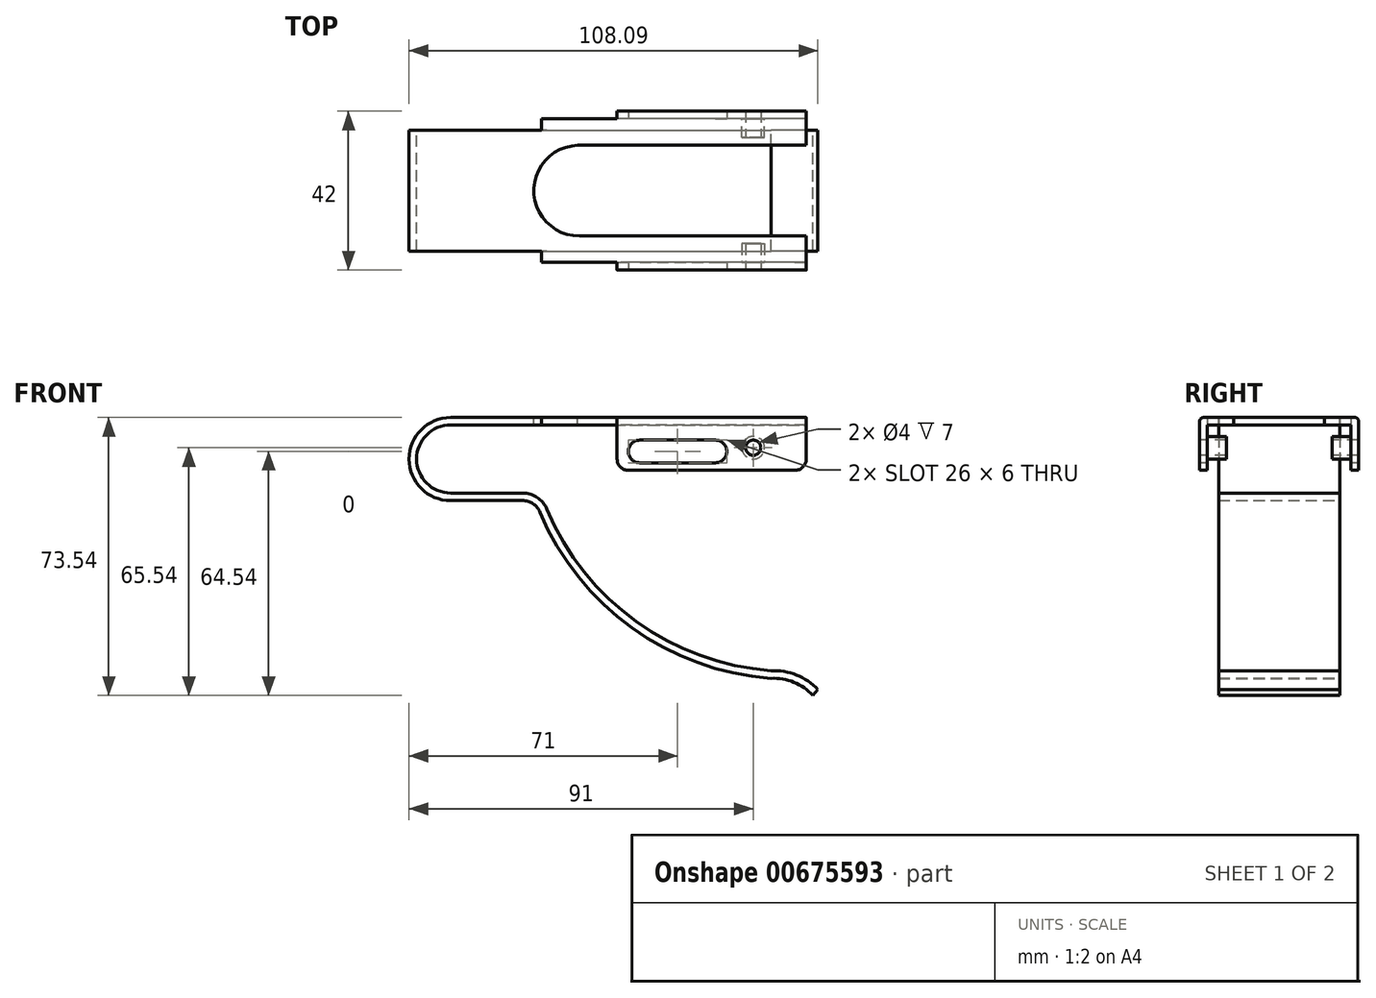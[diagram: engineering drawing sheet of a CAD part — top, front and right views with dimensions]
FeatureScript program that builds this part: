
annotation { "Feature Type Name" : "Feature", "Feature Type Description" : "" }
export const myFeature = defineFeature(function(context is Context, id is Id, definition is map)
    precondition{}
    {
        {
            var Q0;
            Q0=qCreatedBy(makeId("Front.planeOp"),FACE);
            var sketch = newSketch(context, id + "F0", { "sketchPlane" : qUnion([Q0])});
            skArc(sketch, "E0", {"start": v(0, 11) * mm, "mid": v(-11, 0) * mm, "end": v(0, -11) * mm});
            skLineSegment(sketch, "E1", {"start": v(0, 11) * mm, "end": v(94, 11) * mm});
            skLineSegment(sketch, "E2", {"start": v(0, -11) * mm, "end": v(19, -11) * mm});
            skArc(sketch, "E3", {"start": v(23.61, -14.06) * mm, "mid": v(47.95, -44.65) * mm, "end": v(84.68, -58) * mm});
            skArc(sketch, "E4", {"start": v(95.8, -62.54) * mm, "mid": v(90.75, -59.02) * mm, "end": v(84.68, -58) * mm});
            skPoint(sketch, "E5.visualSharp", {"position": v(22.4, -11) * mm});
            skArc(sketch, "E5.filletArc", {"start": v(23.61, -14.06) * mm, "mid": v(21.77, -11.84) * mm, "end": v(19, -11) * mm});
            skLineSegment(sketch, "E6.0", {"start": v(0, 9) * mm, "end": v(94, 9) * mm});
            skArc(sketch, "E6.1", {"start": v(0, 9) * mm, "mid": v(-9, 0) * mm, "end": v(0, -9) * mm});
            skArc(sketch, "E6.2", {"start": v(97.1, -61) * mm, "mid": v(91.45, -57.14) * mm, "end": v(84.7, -56) * mm});
            skArc(sketch, "E6.3", {"start": v(25.45, -13.3) * mm, "mid": v(49.07, -42.99) * mm, "end": v(84.7, -56) * mm});
            skArc(sketch, "E6.4", {"start": v(25.45, -13.3) * mm, "mid": v(22.88, -10.17) * mm, "end": v(19, -9) * mm});
            skLineSegment(sketch, "E6.5", {"start": v(0, -9) * mm, "end": v(19, -9) * mm});
            skLineSegment(sketch, "E7", {"start": v(97.1, -61) * mm, "end": v(110.74, -61) * mm, "construction": true});
            skLineSegment(sketch, "E8", {"start": v(97.1, -61) * mm, "end": v(95.8, -62.54) * mm});
            skLineSegment(sketch, "E9", {"start": v(94, 11) * mm, "end": v(94, 9) * mm});
            skSolve(sketch);
        }
        {
            var Q0;
            Q0 = qSketchRegion(id + "F0", true);
            extrude(context, id + "F1", {"entities" : qUnion([Q0]), "depth" : 16 * mm, "offsetDistance" : 25 * mm});
        }
        {
            var Q0;
            Q0=makeQuery(id+"F1.opExtrude","SWEPT_FACE",FACE,{"disambiguationData":[OSD([sQuery(id+"F0.wireOp",EDGE,"E1")])]});
            var sketch = newSketch(context, id + "F2", { "sketchPlane" : qUnion([Q0])});
            skLineSegment(sketch, "E10.bottom", {"start": v(94, -16) * mm, "end": v(24, -16) * mm});
            skLineSegment(sketch, "E10.top", {"start": v(94, -19) * mm, "end": v(24, -19) * mm});
            skLineSegment(sketch, "E10.left", {"start": v(94, -16) * mm, "end": v(94, -19) * mm});
            skLineSegment(sketch, "E10.right", {"start": v(24, -16) * mm, "end": v(24, -19) * mm});
            skSolve(sketch);
        }
        {
            var Q0;
            Q0 = qSketchRegion(id + "F2", true);
            extrude(context, id + "F3", {"entities" : qUnion([Q0]), "operationType" : NewBodyOperationType.ADD, "oppositeDirection" : true, "depth" : 2 * mm, "offsetDistance" : 25 * mm});
        }
        {
            var Q0;
            Q0=makeQuery(id+"F3.opExtrude","SWEPT_FACE",FACE,{"disambiguationData":[OSD([sQuery(id+"F2.wireOp",EDGE,"E10.top")])]});
            var sketch = newSketch(context, id + "F4", { "sketchPlane" : qUnion([Q0])});
            skLineSegment(sketch, "E11.bottom", {"start": v(94, 11) * mm, "end": v(44, 11) * mm});
            skLineSegment(sketch, "E11.top", {"start": v(94, -3) * mm, "end": v(44, -3) * mm});
            skLineSegment(sketch, "E11.left", {"start": v(94, 11) * mm, "end": v(94, -3) * mm});
            skLineSegment(sketch, "E11.right", {"start": v(44, 11) * mm, "end": v(44, -3) * mm});
            skSolve(sketch);
        }
        {
            var Q0;
            Q0 = qSketchRegion(id + "F4", true);
            extrude(context, id + "F5", {"entities" : qUnion([Q0]), "operationType" : NewBodyOperationType.ADD, "depth" : 2 * mm, "offsetDistance" : 25 * mm});
        }
        {
            var Q0;
            Q0=makeQuery(id+"F5.opExtrude","CAP_EDGE",EDGE,{"disambiguationData":[OSD([sQuery(id+"F4.wireOp",EDGE,"E11.bottom")])],"isStart":false});
            fillet(context, id + "F6", {"entities" : qUnion([Q0]), "radius" : 1 * mm, "tangentPropagation" : true, "allowEdgeOverflow" : false});
        }
        {
            var Q0;
            Q0=makeQuery(id+"F1.opExtrude","SWEPT_BODY",BODY,{"disambiguationData":[OSD([sQuery(id+"F0.wireOp",EDGE,"E0"),sQuery(id+"F0.wireOp",EDGE,"E1"),sQuery(id+"F0.wireOp",EDGE,"E2"),sQuery(id+"F0.wireOp",EDGE,"E3"),sQuery(id+"F0.wireOp",EDGE,"E4"),sQuery(id+"F0.wireOp",EDGE,"E5.filletArc"),sQuery(id+"F0.wireOp",EDGE,"E6.0"),sQuery(id+"F0.wireOp",EDGE,"E6.1"),sQuery(id+"F0.wireOp",EDGE,"E6.2"),sQuery(id+"F0.wireOp",EDGE,"E6.3"),sQuery(id+"F0.wireOp",EDGE,"E6.4"),sQuery(id+"F0.wireOp",EDGE,"E6.5"),sQuery(id+"F0.wireOp",EDGE,"E8"),sQuery(id+"F0.wireOp",EDGE,"E9")])]});
            var Q1;
            Q1=qCreatedBy(makeId("Front.planeOp"),FACE);
            mirror(context, id + "F7", {"operationType" : NewBodyOperationType.ADD, "entities" : qUnion([Q0]), "mirrorPlane" : qUnion([Q1])});
        }
        {
            var Q0;
            {var subQ0=makeQuery(id+"F5.boolean.opBoolean","MERGE",FACE,{"derivedFrom":[makeQuery(id+"F3.boolean.opBoolean","MERGE",FACE,{"derivedFrom":[makeQuery(id+"F1.opExtrude","SWEPT_FACE",FACE,{"disambiguationData":[OSD([sQuery(id+"F0.wireOp",EDGE,"E1")])]}),makeQuery(id+"F3.opExtrude","CAP_FACE",FACE,{"disambiguationData":[OSD([sQuery(id+"F2.wireOp",EDGE,"E10.bottom"),sQuery(id+"F2.wireOp",EDGE,"E10.top"),sQuery(id+"F2.wireOp",EDGE,"E10.left"),sQuery(id+"F2.wireOp",EDGE,"E10.right")])],"isStart":true})]}),makeQuery(id+"F5.opExtrude","SWEPT_FACE",FACE,{"disambiguationData":[OSD([sQuery(id+"F4.wireOp",EDGE,"E11.bottom")])]})]});Q0=makeQuery(id+"F7.boolean.opBoolean","MERGE",FACE,{"derivedFrom":[subQ0,makeQuery(id+"F7.opPattern","COPY",FACE,{"derivedFrom":subQ0,"instanceName":"1"})]});}
            var sketch = newSketch(context, id + "F8", { "sketchPlane" : qUnion([Q0])});
            skArc(sketch, "E12", {"start": v(33.59, 12) * mm, "mid": v(22, -0.2) * mm, "end": v(34, -12) * mm});
            skLineSegment(sketch, "E13", {"start": v(34, -12) * mm, "end": v(94, -12) * mm});
            skLineSegment(sketch, "E14", {"start": v(33.59, 12) * mm, "end": v(94, 12) * mm});
            skSolve(sketch);
        }
        {
            var Q0;
            Q0 = qSketchRegion(id + "F8", true);
            var Q1;
            Q1=makeQuery(id+"F8.imprint","IMPRINT",FACE,{"disambiguationData":[TD([[makeQuery(id+"F8.imprint","IMPRINT",EDGE,{"derivedFrom":sQuery(id+"F8.wireOp",EDGE,"E12")}),1.0]])]});
            extrude(context, id + "F9", {"entities" : qUnion([Q0, Q1]), "operationType" : NewBodyOperationType.REMOVE, "oppositeDirection" : true, "depth" : 2 * mm, "offsetDistance" : 25 * mm});
        }
        {
            var Q0;
            Q0=makeQuery(id+"F5.opExtrude","CAP_FACE",FACE,{"disambiguationData":[OSD([sQuery(id+"F4.wireOp",EDGE,"E11.bottom"),sQuery(id+"F4.wireOp",EDGE,"E11.top"),sQuery(id+"F4.wireOp",EDGE,"E11.left"),sQuery(id+"F4.wireOp",EDGE,"E11.right")])],"isStart":false});
            var sketch = newSketch(context, id + "F10", { "sketchPlane" : qUnion([Q0])});
            skLineSegment(sketch, "E15", {"start": v(50, 2) * mm, "end": v(70, 2) * mm});
            skArc(sketch, "E16.0.startCap", {"start": v(50, -1) * mm, "mid": v(47, 2) * mm, "end": v(50, 5) * mm});
            skArc(sketch, "E16.0.endCap", {"start": v(70, 5) * mm, "mid": v(73, 2) * mm, "end": v(70, -1) * mm});
            skLineSegment(sketch, "E16.0.left", {"start": v(50, 5) * mm, "end": v(70, 5) * mm});
            skLineSegment(sketch, "E16.0.right", {"start": v(50, -1) * mm, "end": v(70, -1) * mm});
            skSolve(sketch);
        }
        {
            var Q0;
            Q0 = qSketchRegion(id + "F10", true);
            extrude(context, id + "F11", {"entities" : qUnion([Q0]), "operationType" : NewBodyOperationType.REMOVE, "endBound" : BoundingType.THROUGH_ALL, "oppositeDirection" : true, "depth" : 25 * mm, "offsetDistance" : 25 * mm});
        }
        {
            var Q0;
            Q0=makeQuery(id+"F5.opExtrude","CAP_FACE",FACE,{"disambiguationData":[OSD([sQuery(id+"F4.wireOp",EDGE,"E11.bottom"),sQuery(id+"F4.wireOp",EDGE,"E11.top"),sQuery(id+"F4.wireOp",EDGE,"E11.left"),sQuery(id+"F4.wireOp",EDGE,"E11.right")])],"isStart":false});
            var sketch = newSketch(context, id + "F12", { "sketchPlane" : qUnion([Q0])});
            skPoint(sketch, "E17", {"position": v(80, 3) * mm});
            skSolve(sketch);
        }
        {
            var Q0;
            Q0=sQuery(id+"F12.wireOp",VERTEX,"E17");
            var Q1;
            Q1=makeQuery(id+"F1.opExtrude","SWEPT_BODY",BODY,{"disambiguationData":[OSD([sQuery(id+"F0.wireOp",EDGE,"E0"),sQuery(id+"F0.wireOp",EDGE,"E1"),sQuery(id+"F0.wireOp",EDGE,"E2"),sQuery(id+"F0.wireOp",EDGE,"E3"),sQuery(id+"F0.wireOp",EDGE,"E4"),sQuery(id+"F0.wireOp",EDGE,"E5.filletArc"),sQuery(id+"F0.wireOp",EDGE,"E6.0"),sQuery(id+"F0.wireOp",EDGE,"E6.1"),sQuery(id+"F0.wireOp",EDGE,"E6.2"),sQuery(id+"F0.wireOp",EDGE,"E6.3"),sQuery(id+"F0.wireOp",EDGE,"E6.4"),sQuery(id+"F0.wireOp",EDGE,"E6.5"),sQuery(id+"F0.wireOp",EDGE,"E8"),sQuery(id+"F0.wireOp",EDGE,"E9")])]});
            hole(context, id + "F13", {"style" : HoleStyle.SIMPLE, "endStyle" : HoleEndStyle.THROUGH, "holeDiameter" : 4 * mm, "majorDiameter" : 5 * mm, "isTappedThrough" : true, "tappedDepth" : 12 * mm, "tapClearance" : 3, "locations" : qUnion([Q0]), "scope" : qUnion([Q1])});
        }
        {
            var Q0;
            Q0=makeQuery(id+"F5.opExtrude","CAP_FACE",FACE,{"disambiguationData":[OSD([sQuery(id+"F4.wireOp",EDGE,"E11.bottom"),sQuery(id+"F4.wireOp",EDGE,"E11.top"),sQuery(id+"F4.wireOp",EDGE,"E11.left"),sQuery(id+"F4.wireOp",EDGE,"E11.right")])],"isStart":true});
            var sketch = newSketch(context, id + "F14", { "sketchPlane" : qUnion([Q0])});
            skCircle(sketch, "E18.0", {"center": v(-80, 3) * mm, "radius": 2 * mm});
            skCircle(sketch, "E19.0", {"center": v(-80, 3) * mm, "radius": 3 * mm});
            skSolve(sketch);
        }
        {
            var Q0;
            Q0 = qSketchRegion(id + "F14", true);
            extrude(context, id + "F15", {"entities" : qUnion([Q0]), "operationType" : NewBodyOperationType.ADD, "depth" : 5 * mm, "offsetDistance" : 25 * mm});
        }
        {
            var Q0;
            Q0=makeQuery(id+"F1.opExtrude","SWEPT_BODY",BODY,{"disambiguationData":[OSD([sQuery(id+"F0.wireOp",EDGE,"E0"),sQuery(id+"F0.wireOp",EDGE,"E1"),sQuery(id+"F0.wireOp",EDGE,"E2"),sQuery(id+"F0.wireOp",EDGE,"E3"),sQuery(id+"F0.wireOp",EDGE,"E4"),sQuery(id+"F0.wireOp",EDGE,"E5.filletArc"),sQuery(id+"F0.wireOp",EDGE,"E6.0"),sQuery(id+"F0.wireOp",EDGE,"E6.1"),sQuery(id+"F0.wireOp",EDGE,"E6.2"),sQuery(id+"F0.wireOp",EDGE,"E6.3"),sQuery(id+"F0.wireOp",EDGE,"E6.4"),sQuery(id+"F0.wireOp",EDGE,"E6.5"),sQuery(id+"F0.wireOp",EDGE,"E8"),sQuery(id+"F0.wireOp",EDGE,"E9")])]});
            var Q1;
            Q1=qCreatedBy(makeId("Front.planeOp"),FACE);
            mirror(context, id + "F16", {"operationType" : NewBodyOperationType.ADD, "entities" : qUnion([Q0]), "mirrorPlane" : qUnion([Q1])});
        }
        {
            var Q0;
            Q0=makeQuery(id+"F5.opExtrude","SWEPT_EDGE",EDGE,{"disambiguationData":[OSD([sQuery(id+"F4.wireOp",EDGE,"E11.top"),sQuery(id+"F4.wireOp",EDGE,"E11.left")])]});
            var Q1;
            Q1=makeQuery(id+"F5.opExtrude","SWEPT_EDGE",EDGE,{"disambiguationData":[OSD([sQuery(id+"F4.wireOp",EDGE,"E11.top"),sQuery(id+"F4.wireOp",EDGE,"E11.right")])]});
            var Q2;
            Q2=makeQuery(id+"F7.opPattern","COPY",EDGE,{"derivedFrom":makeQuery(id+"F5.opExtrude","SWEPT_EDGE",EDGE,{"disambiguationData":[OSD([sQuery(id+"F4.wireOp",EDGE,"E11.top"),sQuery(id+"F4.wireOp",EDGE,"E11.left")])]}),"instanceName":"1"});
            var Q3;
            Q3=makeQuery(id+"F7.opPattern","COPY",EDGE,{"derivedFrom":makeQuery(id+"F5.opExtrude","SWEPT_EDGE",EDGE,{"disambiguationData":[OSD([sQuery(id+"F4.wireOp",EDGE,"E11.top"),sQuery(id+"F4.wireOp",EDGE,"E11.right")])]}),"instanceName":"1"});
            fillet(context, id + "F17", {"entities" : qUnion([Q0, Q1, Q2, Q3]), "radius" : 3 * mm, "tangentPropagation" : true, "allowEdgeOverflow" : false});
        }
    });
